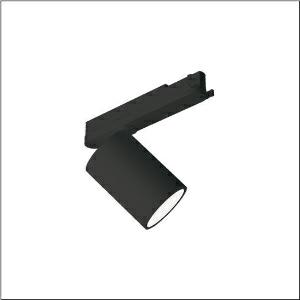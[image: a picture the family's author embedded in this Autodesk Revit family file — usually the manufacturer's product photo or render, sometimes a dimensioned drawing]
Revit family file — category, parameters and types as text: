
# Revit family: spot_31_51sf33mab4b
name_source: partatom
category: Lighting Fixtures
units: mm (PartAtom-declared; Revit-internal decimal feet)

## family parameters
Cut with Voids When Loaded = No
Host = Face
Light Source = No
Part Type = Normal
Room Calculation Point = No
Round Connector Dimension = Use Diameter
Shared = No

## types (1)
- --- (1 x LED, 5030 lm, 41.7 W, 3000K)
    Apparent Load = 42 VA
    CIE Flux Codes = 92 97 99 100 100
    Color Rendering = 90
    Color Temperature = 3000K
    Default Elevation = 1800 mm
    Description = Spot 31, directional spotlight, light control with lens, of PMMA, LED rated luminous flux: 4.830lm, light colour: 930, control gear: ECG Multilumen, with 3-phase adapter, mains connection: 220..240V, AC, 50/60Hz, of aluminium, jet black (RAL 9005), length: 213mm, diameter: 90mm, protection rating (complete): IP20, insulation class (complete): insulation class I (protective earthing), certification: CE, impact resistance: IK02, permissible ambient temperature for indoor applications: -20..+40°C, packaging unit: 1 piece
    Height = 175 mm
    Lamp = 1 x LED
    Lamp Light Flux = 5030 lm
    Lamp Power = 41.7 W
    Lamp count = 1
    Length = 90 mm
    Luminous efficacy = 121 lm/W
    Manufacturer = Siteco
    ModVariant = No
    Model = 51SF33MAB4B
    Mounting Place = Ceiling
    Mounting Type = Pendant
    Number of Poles = 1
    OnlyDefault = Yes
    Power Factor = 1
    Product Name = Spot 31
    Product group = directional spotlight
    ProductGroupID = 905
    Protection Class = Protection class I
    Protection Degree = IP 20
    RLX_Detail_Level = 1
    RLX_Emergency_Light_Flux = 0 lm
    RLX_Emergency_Type = 0
    RLX_Emergency_Type_DB = No
    RlxData = <blob elided: 20881 chars, md5=2a621629>
    Socket = socket
    Standby Power = 0 W
    System Light Flux = 5030 lm
    System Power = 42 W
    Type Comments = factory setting: luminous flux: 100 % | (ON | ON | ON | ON) | 1050 mA
    Type Image = l_1273723.jpg
    URL = http://relux.com
    VarID = @adj_078377
    Voltage = 0 V
    Weight = 0.00 kg
    Width = 0 mm  [stored 0 ft]

note: [stored X ft] marks values corroborated as IEEE doubles in the binary element streams (Revit-internal decimal feet)

## geometry (parser evidence)
native form markers: Blend x4, Sweep x12
no freeform markers — native parametric forms only
